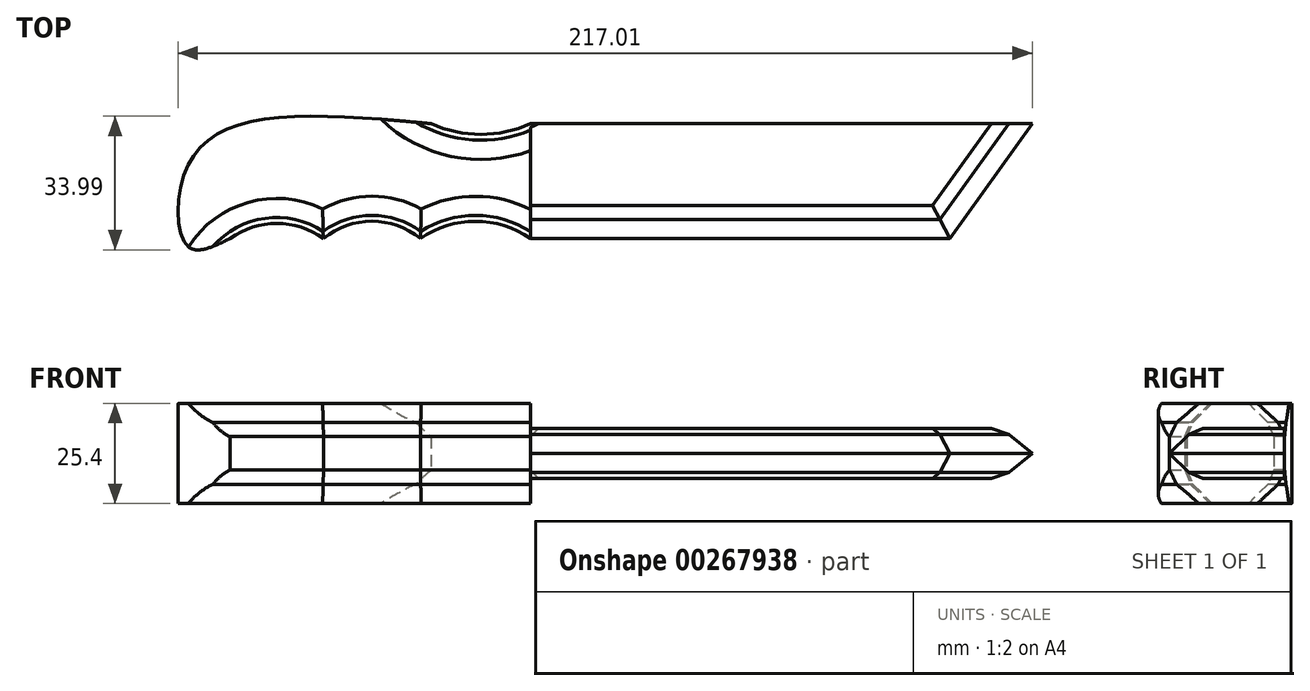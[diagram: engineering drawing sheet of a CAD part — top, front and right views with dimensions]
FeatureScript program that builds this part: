
annotation { "Feature Type Name" : "Feature", "Feature Type Description" : "" }
export const myFeature = defineFeature(function(context is Context, id is Id, definition is map)
    precondition{}
    {
        {
            var Q0;
            Q0=qCreatedBy(makeId("Top.planeOp"),FACE);
            var sketch = newSketch(context, id + "F0", { "sketchPlane" : qUnion([Q0])});
            skLineSegment(sketch, "E0", {"start": v(0, 41.98) * mm, "end": v(127.47, 41.98) * mm});
            skLineSegment(sketch, "E1", {"start": v(127.47, 41.98) * mm, "end": v(106.48, 12.78) * mm});
            skLineSegment(sketch, "E2", {"start": v(106.48, 12.78) * mm, "end": v(0, 12.78) * mm});
            skArc(sketch, "E3", {"start": v(0, 12.78) * mm, "mid": v(-14, 17.15) * mm, "end": v(-27.99, 12.78) * mm});
            skArc(sketch, "E4", {"start": v(-27.99, 12.78) * mm, "mid": v(-40.3, 17.18) * mm, "end": v(-52.63, 12.78) * mm});
            skArc(sketch, "E5", {"start": v(-52.63, 12.78) * mm, "mid": v(-64.5, 16.63) * mm, "end": v(-76.36, 12.78) * mm});
            skArc(sketch, "E6", {"start": v(-25.24, 41.98) * mm, "mid": v(-12.62, 39.24) * mm, "end": v(0, 41.98) * mm});
            skFitSpline(sketch, "E7", {"points": [v(-25.24, 41.98) * mm, v(-73.17, 41.98) * mm, v(-88.08, 28.78) * mm, v(-86.95, 10.67) * mm, v(-76.36, 12.78) * mm], "startDerivative": vector(-148.24, 13.52) * mm, "endDerivative": vector(70.84, 34.74) * mm});
            skLineSegment(sketch, "E8", {"start": v(0, 41.98) * mm, "end": v(0, 12.78) * mm});
            skSolve(sketch);
        }
        {
            var Q0;
            Q0=makeQuery(id+"F0.imprint","IMPRINT",FACE,{"disambiguationData":[TD([[makeQuery(id+"F0.imprint","IMPRINT",EDGE,{"derivedFrom":sQuery(id+"F0.wireOp",EDGE,"E0")}),-1.0]])]});
            extrude(context, id + "F1", {"entities" : qUnion([Q0]), "depth" : 6.35 * mm, "hasSecondDirection" : true, "secondDirectionOppositeDirection" : true, "secondDirectionDepth" : 6.35 * mm});
        }
        {
            var Q0;
            Q0=makeQuery(id+"F0.imprint","IMPRINT",FACE,{"disambiguationData":[TD([[makeQuery(id+"F0.imprint","IMPRINT",EDGE,{"derivedFrom":sQuery(id+"F0.wireOp",EDGE,"E3")}),-1.0]])]});
            extrude(context, id + "F2", {"entities" : qUnion([Q0]), "operationType" : NewBodyOperationType.ADD, "depth" : 12.7 * mm, "hasSecondDirection" : true, "secondDirectionOppositeDirection" : true, "secondDirectionDepth" : 12.7 * mm});
        }
        {
            var Q0;
            Q0=makeQuery(id+"F1.opExtrude","CAP_EDGE",EDGE,{"disambiguationData":[OSD([sQuery(id+"F0.wireOp",EDGE,"E2")])],"isStart":false});
            var Q1;
            Q1=makeQuery(id+"F1.opExtrude","CAP_EDGE",EDGE,{"disambiguationData":[OSD([sQuery(id+"F0.wireOp",EDGE,"E1")])],"isStart":false});
            var Q2;
            Q2=makeQuery(id+"F1.opExtrude","CAP_EDGE",EDGE,{"disambiguationData":[OSD([sQuery(id+"F0.wireOp",EDGE,"E1")])],"isStart":true});
            var Q3;
            Q3=makeQuery(id+"F1.opExtrude","CAP_EDGE",EDGE,{"disambiguationData":[OSD([sQuery(id+"F0.wireOp",EDGE,"E2")])],"isStart":true});
            chamfer(context, id + "F3", {"entities" : qUnion([Q0, Q1, Q2, Q3]), "width" : 6.35 * mm, "tangentPropagation" : true});
        }
        {
            var Q0;
            Q0=makeQuery(id+"F2.opExtrude","CAP_EDGE",EDGE,{"disambiguationData":[OSD([sQuery(id+"F0.wireOp",EDGE,"E4")])],"isStart":false});
            var Q1;
            Q1=makeQuery(id+"F2.opExtrude","CAP_EDGE",EDGE,{"disambiguationData":[OSD([sQuery(id+"F0.wireOp",EDGE,"E3")])],"isStart":false});
            var Q2;
            Q2=makeQuery(id+"F2.opExtrude","CAP_EDGE",EDGE,{"disambiguationData":[OSD([sQuery(id+"F0.wireOp",EDGE,"E5")])],"isStart":false});
            var Q3;
            Q3=makeQuery(id+"F2.opExtrude","CAP_EDGE",EDGE,{"disambiguationData":[OSD([sQuery(id+"F0.wireOp",EDGE,"E3")])],"isStart":true});
            var Q4;
            Q4=makeQuery(id+"F2.opExtrude","CAP_EDGE",EDGE,{"disambiguationData":[OSD([sQuery(id+"F0.wireOp",EDGE,"E4")])],"isStart":true});
            var Q5;
            Q5=makeQuery(id+"F2.opExtrude","CAP_EDGE",EDGE,{"disambiguationData":[OSD([sQuery(id+"F0.wireOp",EDGE,"E5")])],"isStart":true});
            var Q6;
            Q6=makeQuery(id+"F2.opExtrude","CAP_EDGE",EDGE,{"disambiguationData":[OSD([sQuery(id+"F0.wireOp",EDGE,"E6")])],"isStart":false});
            var Q7;
            Q7=makeQuery(id+"F2.opExtrude","CAP_EDGE",EDGE,{"disambiguationData":[OSD([sQuery(id+"F0.wireOp",EDGE,"E6")])],"isStart":true});
            chamfer(context, id + "F4", {"entities" : qUnion([Q0, Q1, Q2, Q3, Q4, Q5, Q6, Q7]), "width" : 6.35 * mm, "tangentPropagation" : true});
        }
        {
            var Q0;
            {var subQ0=sQuery(id+"F0.wireOp",EDGE,"E3");Q0=makeQuery(id+"F4.opChamfer","BLEND_EDGE",EDGE,{"blendedFrom":[makeQuery(id+"F2.opExtrude","CAP_EDGE",EDGE,{"disambiguationData":[OSD([subQ0])],"isStart":false}),makeQuery(id+"F2.opExtrude","SWEPT_FACE",FACE,{"disambiguationData":[OSD([subQ0])]})],"blendedInto":[makeQuery(id+"F2.opExtrude","SWEPT_FACE",FACE,{"disambiguationData":[OSD([subQ0])]})]});}
            var Q1;
            {var subQ0=sQuery(id+"F0.wireOp",EDGE,"E4");Q1=makeQuery(id+"F4.opChamfer","BLEND_EDGE",EDGE,{"blendedFrom":[makeQuery(id+"F2.opExtrude","CAP_EDGE",EDGE,{"disambiguationData":[OSD([subQ0])],"isStart":false}),makeQuery(id+"F2.opExtrude","SWEPT_FACE",FACE,{"disambiguationData":[OSD([subQ0])]})],"blendedInto":[makeQuery(id+"F2.opExtrude","SWEPT_FACE",FACE,{"disambiguationData":[OSD([subQ0])]})]});}
            var Q2;
            {var subQ0=sQuery(id+"F0.wireOp",EDGE,"E5");Q2=makeQuery(id+"F4.opChamfer","BLEND_EDGE",EDGE,{"blendedFrom":[makeQuery(id+"F2.opExtrude","CAP_EDGE",EDGE,{"disambiguationData":[OSD([subQ0])],"isStart":false}),makeQuery(id+"F2.opExtrude","SWEPT_FACE",FACE,{"disambiguationData":[OSD([subQ0])]})],"blendedInto":[makeQuery(id+"F2.opExtrude","SWEPT_FACE",FACE,{"disambiguationData":[OSD([subQ0])]})]});}
            var Q3;
            {var subQ0=sQuery(id+"F0.wireOp",EDGE,"E5");Q3=makeQuery(id+"F4.opChamfer","BLEND_EDGE",EDGE,{"blendedFrom":[makeQuery(id+"F2.opExtrude","CAP_EDGE",EDGE,{"disambiguationData":[OSD([subQ0])],"isStart":true}),makeQuery(id+"F2.opExtrude","SWEPT_FACE",FACE,{"disambiguationData":[OSD([subQ0])]})],"blendedInto":[makeQuery(id+"F2.opExtrude","SWEPT_FACE",FACE,{"disambiguationData":[OSD([subQ0])]})]});}
            var Q4;
            {var subQ0=sQuery(id+"F0.wireOp",EDGE,"E4");Q4=makeQuery(id+"F4.opChamfer","BLEND_EDGE",EDGE,{"blendedFrom":[makeQuery(id+"F2.opExtrude","CAP_EDGE",EDGE,{"disambiguationData":[OSD([subQ0])],"isStart":true}),makeQuery(id+"F2.opExtrude","SWEPT_FACE",FACE,{"disambiguationData":[OSD([subQ0])]})],"blendedInto":[makeQuery(id+"F2.opExtrude","SWEPT_FACE",FACE,{"disambiguationData":[OSD([subQ0])]})]});}
            var Q5;
            {var subQ0=sQuery(id+"F0.wireOp",EDGE,"E3");Q5=makeQuery(id+"F4.opChamfer","BLEND_EDGE",EDGE,{"blendedFrom":[makeQuery(id+"F2.opExtrude","CAP_EDGE",EDGE,{"disambiguationData":[OSD([subQ0])],"isStart":true}),makeQuery(id+"F2.opExtrude","SWEPT_FACE",FACE,{"disambiguationData":[OSD([subQ0])]})],"blendedInto":[makeQuery(id+"F2.opExtrude","SWEPT_FACE",FACE,{"disambiguationData":[OSD([subQ0])]})]});}
            var Q6;
            {var subQ0=sQuery(id+"F0.wireOp",EDGE,"E6");Q6=makeQuery(id+"F4.opChamfer","BLEND_EDGE",EDGE,{"blendedFrom":[makeQuery(id+"F2.opExtrude","CAP_EDGE",EDGE,{"disambiguationData":[OSD([subQ0])],"isStart":false}),makeQuery(id+"F2.opExtrude","SWEPT_FACE",FACE,{"disambiguationData":[OSD([subQ0])]})],"blendedInto":[makeQuery(id+"F2.opExtrude","SWEPT_FACE",FACE,{"disambiguationData":[OSD([subQ0])]})]});}
            var Q7;
            {var subQ0=sQuery(id+"F0.wireOp",EDGE,"E6");Q7=makeQuery(id+"F4.opChamfer","BLEND_EDGE",EDGE,{"blendedFrom":[makeQuery(id+"F2.opExtrude","CAP_EDGE",EDGE,{"disambiguationData":[OSD([subQ0])],"isStart":true}),makeQuery(id+"F2.opExtrude","SWEPT_FACE",FACE,{"disambiguationData":[OSD([subQ0])]})],"blendedInto":[makeQuery(id+"F2.opExtrude","SWEPT_FACE",FACE,{"disambiguationData":[OSD([subQ0])]})]});}
            chamfer(context, id + "F5", {"entities" : qUnion([Q0, Q1, Q2, Q3, Q4, Q5, Q6, Q7]), "width" : 5.08 * mm, "tangentPropagation" : true});
        }
        {
            var Q0;
            {var subQ0=sQuery(id+"F0.wireOp",EDGE,"E1");Q0=makeQuery(id+"F3.opChamfer","BLEND_EDGE",EDGE,{"blendedFrom":[makeQuery(id+"F1.opExtrude","CAP_EDGE",EDGE,{"disambiguationData":[OSD([subQ0])],"isStart":true}),makeQuery(id+"F1.opExtrude","CAP_FACE",FACE,{"disambiguationData":[OSD([sQuery(id+"F0.wireOp",EDGE,"E0"),subQ0,sQuery(id+"F0.wireOp",EDGE,"E2"),sQuery(id+"F0.wireOp",EDGE,"E8")])],"isStart":true})],"blendedInto":[makeQuery(id+"F1.opExtrude","CAP_FACE",FACE,{"disambiguationData":[OSD([sQuery(id+"F0.wireOp",EDGE,"E0"),subQ0,sQuery(id+"F0.wireOp",EDGE,"E2"),sQuery(id+"F0.wireOp",EDGE,"E8")])],"isStart":true})]});}
            var Q1;
            {var subQ0=sQuery(id+"F0.wireOp",EDGE,"E2");Q1=makeQuery(id+"F3.opChamfer","BLEND_EDGE",EDGE,{"blendedFrom":[makeQuery(id+"F1.opExtrude","CAP_EDGE",EDGE,{"disambiguationData":[OSD([subQ0])],"isStart":true}),makeQuery(id+"F1.opExtrude","CAP_FACE",FACE,{"disambiguationData":[OSD([sQuery(id+"F0.wireOp",EDGE,"E0"),sQuery(id+"F0.wireOp",EDGE,"E1"),subQ0,sQuery(id+"F0.wireOp",EDGE,"E8")])],"isStart":true})],"blendedInto":[makeQuery(id+"F1.opExtrude","CAP_FACE",FACE,{"disambiguationData":[OSD([sQuery(id+"F0.wireOp",EDGE,"E0"),sQuery(id+"F0.wireOp",EDGE,"E1"),subQ0,sQuery(id+"F0.wireOp",EDGE,"E8")])],"isStart":true})]});}
            var Q2;
            {var subQ0=sQuery(id+"F0.wireOp",EDGE,"E1");Q2=makeQuery(id+"F3.opChamfer","BLEND_EDGE",EDGE,{"blendedFrom":[makeQuery(id+"F1.opExtrude","CAP_EDGE",EDGE,{"disambiguationData":[OSD([subQ0])],"isStart":false}),makeQuery(id+"F1.opExtrude","CAP_FACE",FACE,{"disambiguationData":[OSD([sQuery(id+"F0.wireOp",EDGE,"E0"),subQ0,sQuery(id+"F0.wireOp",EDGE,"E2"),sQuery(id+"F0.wireOp",EDGE,"E8")])],"isStart":false})],"blendedInto":[makeQuery(id+"F1.opExtrude","CAP_FACE",FACE,{"disambiguationData":[OSD([sQuery(id+"F0.wireOp",EDGE,"E0"),subQ0,sQuery(id+"F0.wireOp",EDGE,"E2"),sQuery(id+"F0.wireOp",EDGE,"E8")])],"isStart":false})]});}
            var Q3;
            {var subQ0=sQuery(id+"F0.wireOp",EDGE,"E2");Q3=makeQuery(id+"F3.opChamfer","BLEND_EDGE",EDGE,{"blendedFrom":[makeQuery(id+"F1.opExtrude","CAP_EDGE",EDGE,{"disambiguationData":[OSD([subQ0])],"isStart":false}),makeQuery(id+"F1.opExtrude","CAP_FACE",FACE,{"disambiguationData":[OSD([sQuery(id+"F0.wireOp",EDGE,"E0"),sQuery(id+"F0.wireOp",EDGE,"E1"),subQ0,sQuery(id+"F0.wireOp",EDGE,"E8")])],"isStart":false})],"blendedInto":[makeQuery(id+"F1.opExtrude","CAP_FACE",FACE,{"disambiguationData":[OSD([sQuery(id+"F0.wireOp",EDGE,"E0"),sQuery(id+"F0.wireOp",EDGE,"E1"),subQ0,sQuery(id+"F0.wireOp",EDGE,"E8")])],"isStart":false})]});}
            chamfer(context, id + "F6", {"entities" : qUnion([Q0, Q1, Q2, Q3]), "width" : 5.08 * mm, "tangentPropagation" : true});
        }
    });
